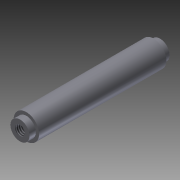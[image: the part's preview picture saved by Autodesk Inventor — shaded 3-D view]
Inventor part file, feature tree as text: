
AUTODESK INVENTOR PART (.ipt)
format: ipt  version: 2012 (Build 160160000, 160)  size: 91,648 bytes
history: native  units: in
note: dims shown in document units (in); Inventor stores cm internally (conversion verified against a paired STEP export)
features: extrude x4, sketch x3, thread x1
ambient origin geometry x8: Origin, YZ Plane, XZ Plane, XY Plane, X Axis, Y Axis, Z Axis, Center Point
bodies: Solid1 (feature_tree)
feature tree (8):
  extrude  "Extrusion1"  Depth=2.75in TaperAngle=0.0deg
  sketch  "Sketch6"  dims[d43=0.19in d44=0.375in]
  extrude  "Extrusion11"  Depth=0.375in
  extrude  "Extrusion12"  Depth=0.125in TaperAngle=0.0deg
  extrude  "Extrusion13"  Depth=0.125in TaperAngle=0.0deg
  thread  "Thread7"  [1 undecoded]
  sketch  "Sketch1"  dims[d0=0.5in d1=2.75in d2=0.0in]
  sketch  "Sketch7"  dims[d45=0.125in d46=0.0in d47=0.125in d48=0.0in d49=0.125in d50=0.0in d51=1.0in d52=0.0in]
note: 1 required parameter value undecoded (feature->parameter linkage not recoverable at this tier; creation-order binding heuristic only, values carry confidence <= 0.55)
